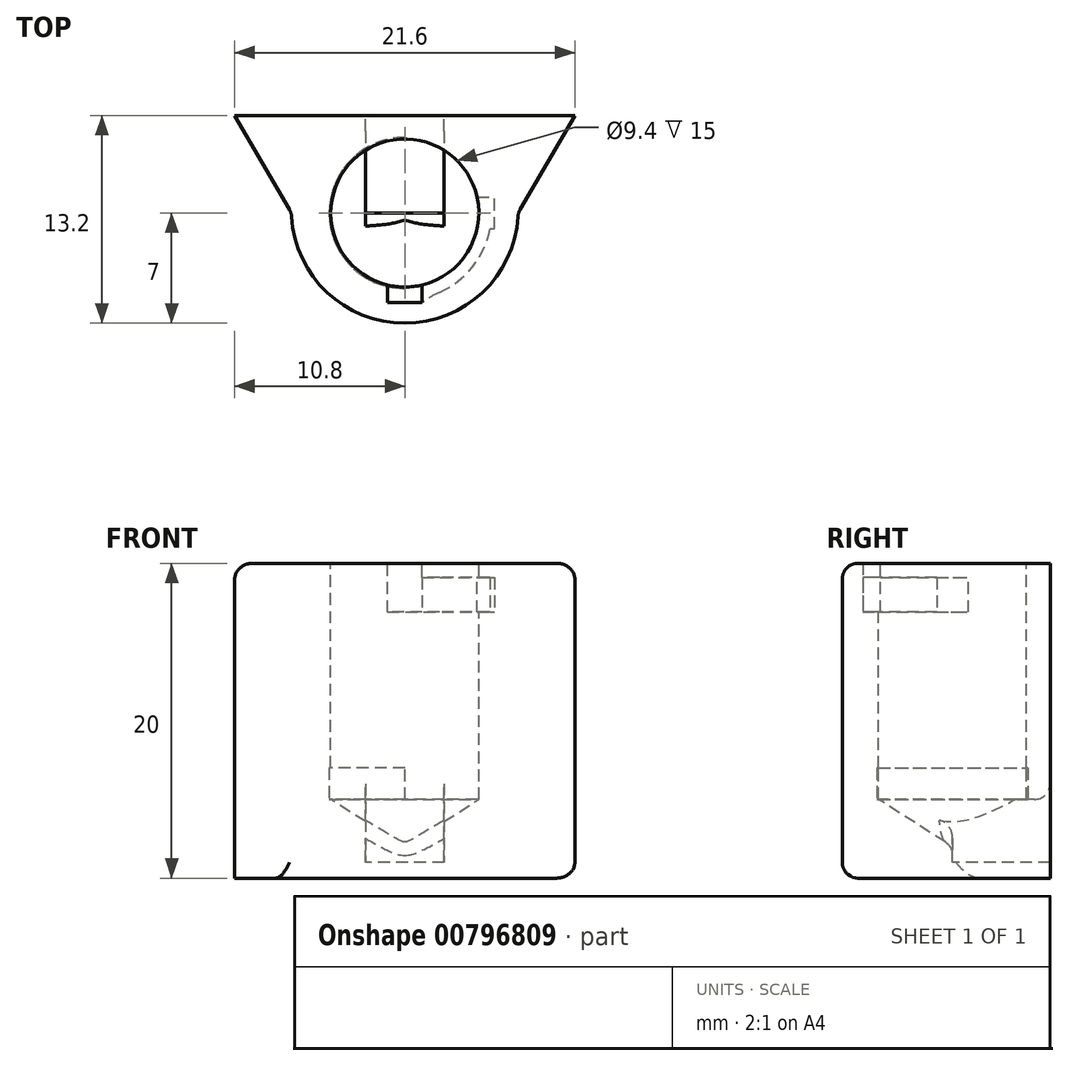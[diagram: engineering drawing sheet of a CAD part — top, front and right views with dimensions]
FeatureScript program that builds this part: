
annotation { "Feature Type Name" : "Feature", "Feature Type Description" : "" }
export const myFeature = defineFeature(function(context is Context, id is Id, definition is map)
    precondition{}
    {
        {
            var Q0;
            Q0=qCreatedBy(makeId("Top.planeOp"),FACE);
            var sketch = newSketch(context, id + "F0", { "sketchPlane" : qUnion([Q0])});
            skArc(sketch, "E0", {"start": v(-7.2, 0) * mm, "mid": v(0, -7) * mm, "end": v(7.2, 0) * mm});
            skLineSegment(sketch, "E1", {"start": v(-10.8, 6.2) * mm, "end": v(-7.2, 0) * mm});
            skLineSegment(sketch, "E2", {"start": v(10.8, 6.2) * mm, "end": v(7.2, 0) * mm});
            skLineSegment(sketch, "E3", {"start": v(-10.8, 6.2) * mm, "end": v(10.8, 6.2) * mm});
            skSolve(sketch);
        }
        {
            var Q0;
            Q0=makeQuery(id+"F0.imprint","IMPRINT",FACE,{"disambiguationData":[TD([[makeQuery(id+"F0.imprint","IMPRINT",EDGE,{"derivedFrom":sQuery(id+"F0.wireOp",EDGE,"E0")}),1.0]])]});
            extrude(context, id + "F1", {"entities" : qUnion([Q0]), "depth" : 15 * mm, "offsetDistance" : 25 * mm});
        }
        {
            var Q0;
            Q0=makeQuery(id+"F0.imprint","IMPRINT",FACE,{"disambiguationData":[TD([[makeQuery(id+"F0.imprint","IMPRINT",EDGE,{"derivedFrom":sQuery(id+"F0.wireOp",EDGE,"E0")}),1.0]])]});
            extrude(context, id + "F2", {"entities" : qUnion([Q0]), "operationType" : NewBodyOperationType.ADD, "oppositeDirection" : true, "depth" : 5 * mm, "offsetDistance" : 25 * mm});
        }
        {
            var Q0;
            {var subQ0=sQuery(id+"F0.wireOp",EDGE,"E2");var subQ1=sQuery(id+"F0.wireOp",EDGE,"E0");Q0=makeQuery(id+"F2.boolean.opBoolean","MERGE",EDGE,{"derivedFrom":[makeQuery(id+"F1.opExtrude","SWEPT_EDGE",EDGE,{"disambiguationData":[OSD([subQ1,subQ0])]}),makeQuery(id+"F2.opExtrude","SWEPT_EDGE",EDGE,{"disambiguationData":[OSD([subQ1,subQ0])]})]});}
            var Q1;
            Q1=makeQuery(id+"F1.opExtrude","CAP_EDGE",EDGE,{"disambiguationData":[OSD([sQuery(id+"F0.wireOp",EDGE,"E0")])],"isStart":false});
            var Q2;
            Q2=makeQuery(id+"F1.opExtrude","CAP_EDGE",EDGE,{"disambiguationData":[OSD([sQuery(id+"F0.wireOp",EDGE,"E2")])],"isStart":false});
            var Q3;
            Q3=makeQuery(id+"F1.opExtrude","CAP_EDGE",EDGE,{"disambiguationData":[OSD([sQuery(id+"F0.wireOp",EDGE,"E1")])],"isStart":false});
            var Q4;
            Q4=makeQuery(id+"F2.opExtrude","CAP_EDGE",EDGE,{"disambiguationData":[OSD([sQuery(id+"F0.wireOp",EDGE,"E2")])],"isStart":false});
            var Q5;
            Q5=makeQuery(id+"F2.opExtrude","CAP_EDGE",EDGE,{"disambiguationData":[OSD([sQuery(id+"F0.wireOp",EDGE,"E0")])],"isStart":false});
            var Q6;
            {var subQ0=sQuery(id+"F0.wireOp",EDGE,"E1");var subQ1=sQuery(id+"F0.wireOp",EDGE,"E0");Q6=makeQuery(id+"F2.boolean.opBoolean","MERGE",EDGE,{"derivedFrom":[makeQuery(id+"F1.opExtrude","SWEPT_EDGE",EDGE,{"disambiguationData":[OSD([subQ1,subQ0])]}),makeQuery(id+"F2.opExtrude","SWEPT_EDGE",EDGE,{"disambiguationData":[OSD([subQ1,subQ0])]})]});}
            fillet(context, id + "F3", {"entities" : qUnion([Q0, Q1, Q2, Q3, Q4, Q5, Q6]), "radius" : 1 * mm, "tangentPropagation" : true, "allowEdgeOverflow" : false});
        }
        {
            var Q0;
            Q0=qCreatedBy(makeId("Front.planeOp"),FACE);
            var sketch = newSketch(context, id + "F4", { "sketchPlane" : qUnion([Q0])});
            skLineSegment(sketch, "E4.right", {"start": v(4.7, 0) * mm, "end": v(4.7, 16) * mm});
            skLineSegment(sketch, "E5", {"start": v(0, -3) * mm, "end": v(4.7, 0) * mm});
            skLineSegment(sketch, "E6", {"start": v(0, -3) * mm, "end": v(0, 16) * mm});
            skLineSegment(sketch, "E7", {"start": v(4.7, 16) * mm, "end": v(0, 16) * mm});
            skSolve(sketch);
        }
        {
            var Q0;
            Q0=makeQuery(id+"F4.imprint","IMPRINT",FACE,{"disambiguationData":[TD([[makeQuery(id+"F4.imprint","IMPRINT",EDGE,{"derivedFrom":sQuery(id+"F4.wireOp",EDGE,"E4.right")}),1.0]])]});
            var Q1;
            Q1=sQuery(id+"F4.wireOp",EDGE,"E6");
            revolve(context, id + "F5", {"operationType" : NewBodyOperationType.REMOVE, "surfaceOperationType" : NewSurfaceOperationType.NEW, "entities" : qUnion([Q0]), "axis" : qUnion([Q1]), "revolveType" : RevolveType.FULL, "oppositeDirection" : true});
        }
        {
            var Q0;
            Q0=qCreatedBy(makeId("Right.planeOp"),FACE);
            var sketch = newSketch(context, id + "F6", { "sketchPlane" : qUnion([Q0])});
            skLineSegment(sketch, "E8.bottom", {"start": v(-5.7, 15.9) * mm, "end": v(-3.5, 15.9) * mm});
            skLineSegment(sketch, "E8.top", {"start": v(-5.7, 11.9) * mm, "end": v(-3.5, 11.9) * mm});
            skLineSegment(sketch, "E8.left", {"start": v(-5.7, 15.9) * mm, "end": v(-5.7, 11.9) * mm});
            skLineSegment(sketch, "E8.right", {"start": v(-3.5, 15.9) * mm, "end": v(-3.5, 11.9) * mm});
            skSolve(sketch);
        }
        {
            var Q0;
            Q0=makeQuery(id+"F6.imprint","IMPRINT",FACE,{"disambiguationData":[TD([[makeQuery(id+"F6.imprint","IMPRINT",EDGE,{"derivedFrom":sQuery(id+"F6.wireOp",EDGE,"E8.bottom")}),-1.0]])]});
            extrude(context, id + "F7", {"entities" : qUnion([Q0]), "operationType" : NewBodyOperationType.REMOVE, "endBound" : BoundingType.SYMMETRIC, "depth" : 2.2 * mm, "offsetDistance" : 25 * mm});
        }
        {
            var Q0;
            Q0=qCreatedBy(makeId("Right.planeOp"),FACE);
            var sketch = newSketch(context, id + "F8", { "sketchPlane" : qUnion([Q0])});
            skLineSegment(sketch, "E9.bottom", {"start": v(-5.5, 14.1) * mm, "end": v(0, 14.1) * mm});
            skLineSegment(sketch, "E9.top", {"start": v(-5.5, 11.9) * mm, "end": v(0, 11.9) * mm});
            skLineSegment(sketch, "E9.left", {"start": v(-5.5, 14.1) * mm, "end": v(-5.5, 11.9) * mm});
            skLineSegment(sketch, "E9.right", {"start": v(0, 14.1) * mm, "end": v(0, 11.9) * mm});
            skSolve(sketch);
        }
        {
            var Q0;
            Q0=makeQuery(id+"F8.imprint","IMPRINT",FACE,{"disambiguationData":[TD([[makeQuery(id+"F8.imprint","IMPRINT",EDGE,{"derivedFrom":sQuery(id+"F8.wireOp",EDGE,"E9.bottom")}),-1.0]])]});
            var Q1;
            Q1=sQuery(id+"F8.wireOp",EDGE,"E9.right");
            revolve(context, id + "F9", {"operationType" : NewBodyOperationType.REMOVE, "surfaceOperationType" : NewSurfaceOperationType.NEW, "entities" : qUnion([Q0]), "axis" : qUnion([Q1]), "revolveType" : RevolveType.ONE_DIRECTION, "oppositeDirection" : true, "angle" : 90 * degree});
        }
        {
            var Q0;
            Q0=makeQuery(id+"F9.boolean.opBoolean","INTERSECT",EDGE,{"derivedFrom":[makeQuery(id+"F7.boolean.opBoolean","COPY",FACE,{"derivedFrom":makeQuery(id+"F7.opExtrude","CAP_FACE",FACE,{"disambiguationData":[OSD([sQuery(id+"F6.wireOp",EDGE,"E8.bottom"),sQuery(id+"F6.wireOp",EDGE,"E8.top"),sQuery(id+"F6.wireOp",EDGE,"E8.left"),sQuery(id+"F6.wireOp",EDGE,"E8.right")])],"isStart":false})}),makeQuery(id+"F9.opRevolve","SWEPT_FACE",FACE,{"disambiguationData":[OSD([sQuery(id+"F8.wireOp",EDGE,"E9.left")])]})]});
            fillet(context, id + "F10", {"entities" : qUnion([Q0]), "radius" : 5 * mm, "tangentPropagation" : true, "allowEdgeOverflow" : false});
        }
        {
            var Q0;
            Q0=qCreatedBy(makeId("Front.planeOp"),FACE);
            var sketch = newSketch(context, id + "F11", { "sketchPlane" : qUnion([Q0])});
            skLineSegment(sketch, "E10.bottom", {"start": v(3.5, 14.1) * mm, "end": v(5.7, 14.1) * mm});
            skLineSegment(sketch, "E10.top", {"start": v(3.5, 11.9) * mm, "end": v(5.7, 11.9) * mm});
            skLineSegment(sketch, "E10.left", {"start": v(3.5, 14.1) * mm, "end": v(3.5, 11.9) * mm});
            skLineSegment(sketch, "E10.right", {"start": v(5.7, 14.1) * mm, "end": v(5.7, 11.9) * mm});
            skSolve(sketch);
        }
        {
            var Q0;
            Q0=makeQuery(id+"F11.imprint","IMPRINT",FACE,{"disambiguationData":[TD([[makeQuery(id+"F11.imprint","IMPRINT",EDGE,{"derivedFrom":sQuery(id+"F11.wireOp",EDGE,"E10.bottom")}),-1.0]])]});
            extrude(context, id + "F12", {"entities" : qUnion([Q0]), "operationType" : NewBodyOperationType.REMOVE, "endBound" : BoundingType.SYMMETRIC, "depth" : 2 * mm, "offsetDistance" : 25 * mm});
        }
        {
            var Q0;
            Q0=qCreatedBy(makeId("Right.planeOp"),FACE);
            var sketch = newSketch(context, id + "F13", { "sketchPlane" : qUnion([Q0])});
            skLineSegment(sketch, "E11.bottom", {"start": v(4.6, 0) * mm, "end": v(0, 0) * mm});
            skLineSegment(sketch, "E11.top", {"start": v(4.6, 15) * mm, "end": v(0, 15) * mm});
            skLineSegment(sketch, "E11.left", {"start": v(4.6, 0) * mm, "end": v(4.6, 15) * mm});
            skLineSegment(sketch, "E11.right", {"start": v(0, 0) * mm, "end": v(0, 15) * mm});
            skSolve(sketch);
        }
        {
            var Q0;
            Q0=makeQuery(id+"F13.imprint","IMPRINT",FACE,{"disambiguationData":[TD([[makeQuery(id+"F13.imprint","IMPRINT",EDGE,{"derivedFrom":sQuery(id+"F13.wireOp",EDGE,"E11.bottom")}),-1.0]])]});
            var Q1;
            Q1=sQuery(id+"F13.wireOp",EDGE,"E11.right");
            revolve(context, id + "F14", {"operationType" : NewBodyOperationType.REMOVE, "surfaceOperationType" : NewSurfaceOperationType.NEW, "entities" : qUnion([Q0]), "axis" : qUnion([Q1]), "revolveType" : RevolveType.SYMMETRIC, "angle" : 170 * degree});
        }
        {
            var Q0;
            Q0=qCreatedBy(makeId("Right.planeOp"),FACE);
            var sketch = newSketch(context, id + "F15", { "sketchPlane" : qUnion([Q0])});
            skLineSegment(sketch, "E12.bottom", {"start": v(0, 2) * mm, "end": v(4.8, 2) * mm});
            skLineSegment(sketch, "E12.top", {"start": v(0, 0) * mm, "end": v(4.8, 0) * mm});
            skLineSegment(sketch, "E12.left", {"start": v(0, 2) * mm, "end": v(0, 0) * mm});
            skLineSegment(sketch, "E12.right", {"start": v(4.8, 2) * mm, "end": v(4.8, 0) * mm});
            skSolve(sketch);
        }
        {
            var Q0;
            Q0=makeQuery(id+"F15.imprint","IMPRINT",FACE,{"disambiguationData":[TD([[makeQuery(id+"F15.imprint","IMPRINT",EDGE,{"derivedFrom":sQuery(id+"F15.wireOp",EDGE,"E12.bottom")}),-1.0]])]});
            var Q1;
            Q1=sQuery(id+"F15.wireOp",EDGE,"E12.left");
            revolve(context, id + "F16", {"operationType" : NewBodyOperationType.REMOVE, "surfaceOperationType" : NewSurfaceOperationType.NEW, "entities" : qUnion([Q0]), "axis" : qUnion([Q1]), "revolveType" : RevolveType.ONE_DIRECTION, "oppositeDirection" : true, "angle" : 180 * degree});
        }
        {
            var Q0;
            Q0=qCreatedBy(makeId("Right.planeOp"),FACE);
            var sketch = newSketch(context, id + "F17", { "sketchPlane" : qUnion([Q0])});
            skLineSegment(sketch, "E13.bottom", {"start": v(7.2, -4) * mm, "end": v(0, -4) * mm});
            skLineSegment(sketch, "E13.top", {"start": v(7.2, 0) * mm, "end": v(0, 0) * mm});
            skLineSegment(sketch, "E13.left", {"start": v(7.2, -4) * mm, "end": v(7.2, 0) * mm});
            skLineSegment(sketch, "E13.right", {"start": v(0, -4) * mm, "end": v(0, 0) * mm});
            skSolve(sketch);
        }
        {
            var Q0;
            Q0=makeQuery(id+"F17.imprint","IMPRINT",FACE,{"disambiguationData":[TD([[makeQuery(id+"F17.imprint","IMPRINT",EDGE,{"derivedFrom":sQuery(id+"F17.wireOp",EDGE,"E13.bottom")}),-1.0]])]});
            extrude(context, id + "F18", {"entities" : qUnion([Q0]), "operationType" : NewBodyOperationType.REMOVE, "endBound" : BoundingType.SYMMETRIC, "depth" : 5 * mm, "offsetDistance" : 25 * mm});
        }
        {
            var Q0;
            Q0=makeQuery(id+"F18.boolean.opBoolean","INTERSECT",EDGE,{"disambiguationData":[OD(0.0)],"derivedFrom":[makeQuery(id+"F5.boolean.opBoolean","COPY",FACE,{"derivedFrom":makeQuery(id+"F5.opRevolve","SWEPT_FACE",FACE,{"disambiguationData":[OSD([sQuery(id+"F4.wireOp",EDGE,"E5")])]})}),makeQuery(id+"F18.opExtrude","SWEPT_FACE",FACE,{"disambiguationData":[OSD([sQuery(id+"F17.wireOp",EDGE,"E13.right")])]})]});
            var Q1;
            Q1=makeQuery(id+"F18.boolean.opBoolean","INTERSECT",EDGE,{"disambiguationData":[OD(1.0)],"derivedFrom":[makeQuery(id+"F5.boolean.opBoolean","COPY",FACE,{"derivedFrom":makeQuery(id+"F5.opRevolve","SWEPT_FACE",FACE,{"disambiguationData":[OSD([sQuery(id+"F4.wireOp",EDGE,"E5")])]})}),makeQuery(id+"F18.opExtrude","SWEPT_FACE",FACE,{"disambiguationData":[OSD([sQuery(id+"F17.wireOp",EDGE,"E13.right")])]})]});
            var Q2;
            {var subQ0=sQuery(id+"F0.wireOp",EDGE,"E3");Q2=makeQuery(id+"F18.boolean.opBoolean","INTERSECT",EDGE,{"derivedFrom":[makeQuery(id+"F2.boolean.opBoolean","MERGE",FACE,{"derivedFrom":[makeQuery(id+"F1.opExtrude","SWEPT_FACE",FACE,{"disambiguationData":[OSD([subQ0])]}),makeQuery(id+"F2.opExtrude","SWEPT_FACE",FACE,{"disambiguationData":[OSD([subQ0])]})]}),makeQuery(id+"F18.opExtrude","SWEPT_FACE",FACE,{"disambiguationData":[OSD([sQuery(id+"F17.wireOp",EDGE,"E13.top")])]})]});}
            fillet(context, id + "F19", {"entities" : qUnion([Q0, Q1, Q2]), "radius" : 1 * mm, "allowEdgeOverflow" : false});
        }
    });
